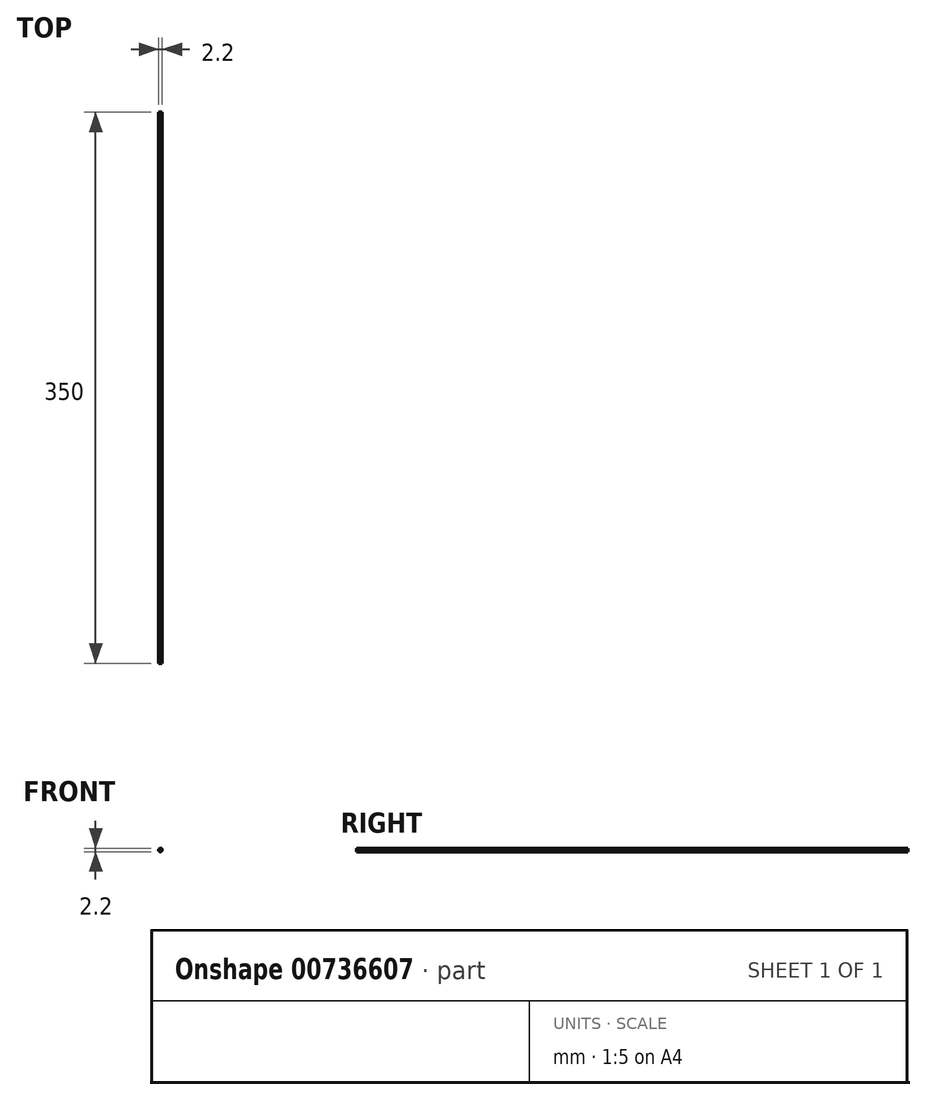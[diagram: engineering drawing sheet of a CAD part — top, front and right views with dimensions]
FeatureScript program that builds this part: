
annotation { "Feature Type Name" : "Feature", "Feature Type Description" : "" }
export const myFeature = defineFeature(function(context is Context, id is Id, definition is map)
    precondition{}
    {
        {
            var Q0;
            Q0=qCreatedBy(makeId("Front.planeOp"),FACE);
            var sketch = newSketch(context, id + "F0", { "sketchPlane" : qUnion([Q0])});
            skCircle(sketch, "E0", {"center": v(0, 0) * mm, "radius": 1.1 * mm});
            skSolve(sketch);
        }
        {
            var Q0;
            Q0 = qSketchRegion(id + "F0", true);
            extrude(context, id + "F1", {"entities" : qUnion([Q0]), "depth" : 350 * mm, "offsetDistance" : 25 * mm, "symmetric" : true});
        }
    });
